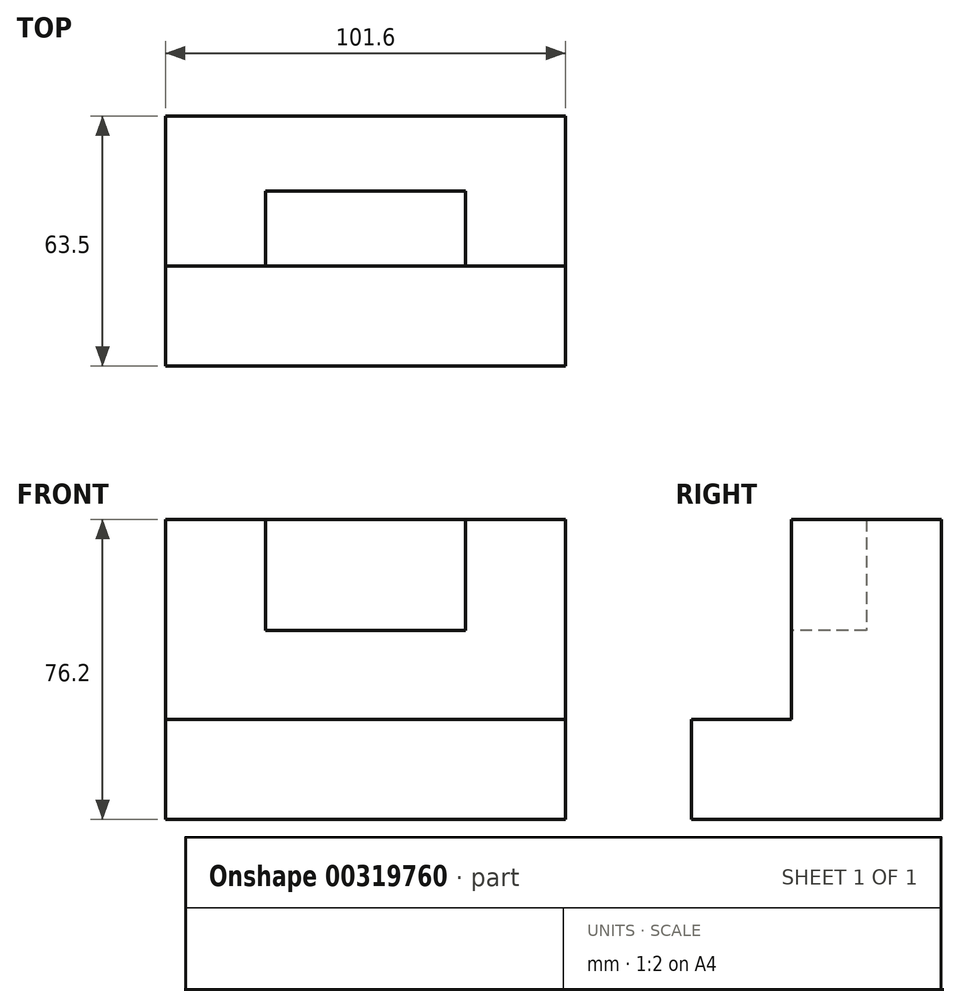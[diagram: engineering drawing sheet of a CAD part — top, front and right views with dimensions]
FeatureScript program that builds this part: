
annotation { "Feature Type Name" : "Feature", "Feature Type Description" : "" }
export const myFeature = defineFeature(function(context is Context, id is Id, definition is map)
    precondition{}
    {
        {
            var Q0;
            Q0=qCreatedBy(makeId("Right.planeOp"),FACE);
            var sketch = newSketch(context, id + "F0", { "sketchPlane" : qUnion([Q0])});
            skLineSegment(sketch, "E0", {"start": v(-5.25, 55.13) * mm, "end": v(32.85, 55.13) * mm});
            skLineSegment(sketch, "E1", {"start": v(32.85, 55.13) * mm, "end": v(32.85, -21.07) * mm});
            skLineSegment(sketch, "E2", {"start": v(32.85, -21.07) * mm, "end": v(-30.65, -21.07) * mm});
            skLineSegment(sketch, "E3", {"start": v(-30.65, -21.07) * mm, "end": v(-30.65, 4.33) * mm});
            skLineSegment(sketch, "E4", {"start": v(-30.65, 4.33) * mm, "end": v(-5.25, 4.33) * mm});
            skLineSegment(sketch, "E5", {"start": v(-5.25, 4.33) * mm, "end": v(-5.25, 55.13) * mm});
            skSolve(sketch);
        }
        {
            var Q0;
            Q0=makeQuery(id+"F0.imprint","IMPRINT",FACE,{"disambiguationData":[TD([[makeQuery(id+"F0.imprint","IMPRINT",EDGE,{"derivedFrom":sQuery(id+"F0.wireOp",EDGE,"E0")}),-1.0]])]});
            extrude(context, id + "F1", {"entities" : qUnion([Q0]), "depth" : 101.6 * mm});
        }
        {
            var Q0;
            Q0=makeQuery(id+"F1.opExtrude","SWEPT_FACE",FACE,{"disambiguationData":[OSD([sQuery(id+"F0.wireOp",EDGE,"E5")])]});
            var sketch = newSketch(context, id + "F2", { "sketchPlane" : qUnion([Q0])});
            skLineSegment(sketch, "E6.bottom", {"start": v(25.4, 55.13) * mm, "end": v(76.2, 55.13) * mm});
            skLineSegment(sketch, "E6.top", {"start": v(25.4, 26.91) * mm, "end": v(76.2, 26.91) * mm});
            skLineSegment(sketch, "E6.left", {"start": v(25.4, 55.13) * mm, "end": v(25.4, 26.91) * mm});
            skLineSegment(sketch, "E6.right", {"start": v(76.2, 55.13) * mm, "end": v(76.2, 26.91) * mm});
            skSolve(sketch);
        }
        {
            var Q0;
            Q0 = qSketchRegion(id + "F2", true);
            extrude(context, id + "F3", {"entities" : qUnion([Q0]), "operationType" : NewBodyOperationType.REMOVE, "oppositeDirection" : true, "depth" : 19.05 * mm});
        }
    });
